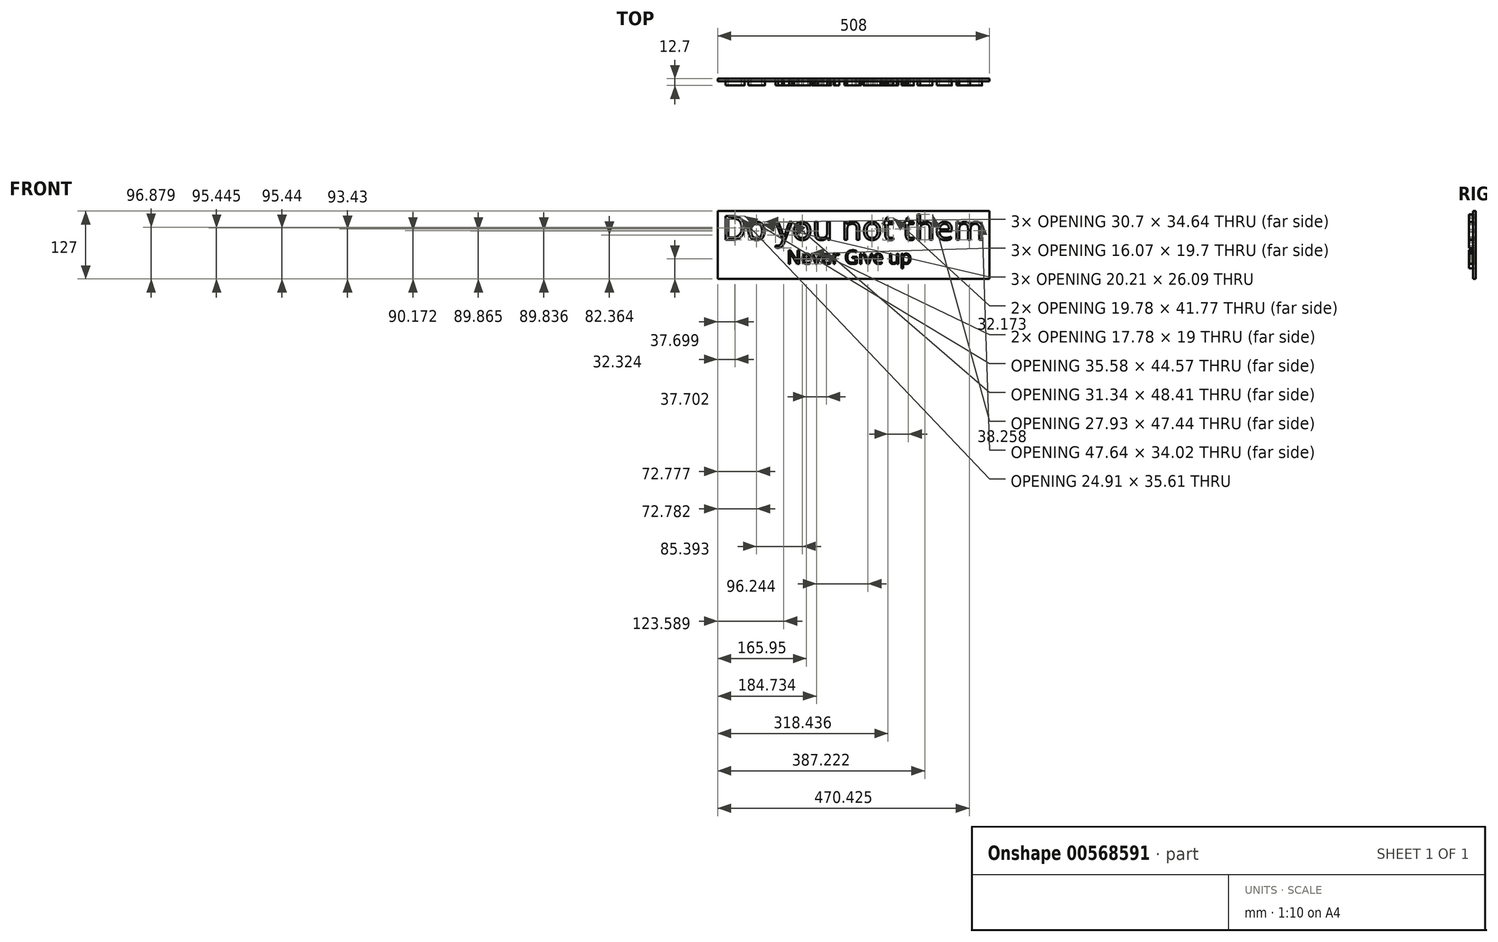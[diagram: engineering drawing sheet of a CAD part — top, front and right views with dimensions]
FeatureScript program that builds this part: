
annotation { "Feature Type Name" : "Feature", "Feature Type Description" : "" }
export const myFeature = defineFeature(function(context is Context, id is Id, definition is map)
    precondition{}
    {
        {
            var Q0;
            Q0=qCreatedBy(makeId("Front.planeOp"),FACE);
            var sketch = newSketch(context, id + "F0", { "sketchPlane" : qUnion([Q0])});
            skLineSegment(sketch, "E0", {"start": v(0, 0) * mm, "end": v(254, 0) * mm});
            skLineSegment(sketch, "E1", {"start": v(0, 0) * mm, "end": v(-254, 0) * mm});
            skLineSegment(sketch, "E2", {"start": v(254, 0) * mm, "end": v(254, 127) * mm});
            skLineSegment(sketch, "E3", {"start": v(254, 127) * mm, "end": v(-254, 127) * mm});
            skLineSegment(sketch, "E4", {"start": v(-254, 0) * mm, "end": v(-254, 127) * mm});
            skText(sketch, "E5", { "text": "Do you not them\n", "fontName": "OpenSans-Regular.ttf"});
            skText(sketch, "E6", { "text": "Never Give up", "fontName": "OpenSans-Regular.ttf"});
            const initialGuessF0  = {"E5": [-0.24559, 0.07316, 1, 0, 0.04495], "E6": [-0.12484, 0.0282, 1, 0, 0.02556]};
            skSetInitialGuess(sketch, initialGuessF0);
            skSolve(sketch);
        }
        {
            var Q0;
            Q0=makeQuery(id+"F0.imprint","IMPRINT",FACE,{"disambiguationData":[TD([[makeQuery(id+"F0.imprint","IMPRINT",EDGE,{"derivedFrom":sQuery(id+"F0.wireOp",EDGE,"E5.sketch_text.stroke-0")}),-1.0]])]});
            var Q1;
            Q1=makeQuery(id+"F0.imprint","IMPRINT",FACE,{"disambiguationData":[TD([[makeQuery(id+"F0.imprint","IMPRINT",EDGE,{"derivedFrom":sQuery(id+"F0.wireOp",EDGE,"E5.sketch_text.stroke-14")}),-1.0]])]});
            var Q2;
            Q2=makeQuery(id+"F0.imprint","IMPRINT",FACE,{"disambiguationData":[TD([[makeQuery(id+"F0.imprint","IMPRINT",EDGE,{"derivedFrom":sQuery(id+"F0.wireOp",EDGE,"E5.sketch_text.stroke-31")}),-1.0]])]});
            var Q3;
            Q3=makeQuery(id+"F0.imprint","IMPRINT",FACE,{"disambiguationData":[TD([[makeQuery(id+"F0.imprint","IMPRINT",EDGE,{"derivedFrom":sQuery(id+"F0.wireOp",EDGE,"E5.sketch_text.stroke-47")}),-1.0]])]});
            var Q4;
            Q4=makeQuery(id+"F0.imprint","IMPRINT",FACE,{"disambiguationData":[TD([[makeQuery(id+"F0.imprint","IMPRINT",EDGE,{"derivedFrom":sQuery(id+"F0.wireOp",EDGE,"E5.sketch_text.stroke-64")}),-1.0]])]});
            var Q5;
            Q5=makeQuery(id+"F0.imprint","IMPRINT",FACE,{"disambiguationData":[TD([[makeQuery(id+"F0.imprint","IMPRINT",EDGE,{"derivedFrom":sQuery(id+"F0.wireOp",EDGE,"E5.sketch_text.stroke-81")}),-1.0]])]});
            var Q6;
            Q6=makeQuery(id+"F0.imprint","IMPRINT",FACE,{"disambiguationData":[TD([[makeQuery(id+"F0.imprint","IMPRINT",EDGE,{"derivedFrom":sQuery(id+"F0.wireOp",EDGE,"E5.sketch_text.stroke-98")}),-1.0]])]});
            var Q7;
            Q7=makeQuery(id+"F0.imprint","IMPRINT",FACE,{"disambiguationData":[TD([[makeQuery(id+"F0.imprint","IMPRINT",EDGE,{"derivedFrom":sQuery(id+"F0.wireOp",EDGE,"E5.sketch_text.stroke-115")}),-1.0]])]});
            var Q8;
            Q8=makeQuery(id+"F0.imprint","IMPRINT",FACE,{"disambiguationData":[TD([[makeQuery(id+"F0.imprint","IMPRINT",EDGE,{"derivedFrom":sQuery(id+"F0.wireOp",EDGE,"E5.sketch_text.stroke-134")}),-1.0]])]});
            var Q9;
            Q9=makeQuery(id+"F0.imprint","IMPRINT",FACE,{"disambiguationData":[TD([[makeQuery(id+"F0.imprint","IMPRINT",EDGE,{"derivedFrom":sQuery(id+"F0.wireOp",EDGE,"E5.sketch_text.stroke-153")}),-1.0]])]});
            var Q10;
            Q10=makeQuery(id+"F0.imprint","IMPRINT",FACE,{"disambiguationData":[TD([[makeQuery(id+"F0.imprint","IMPRINT",EDGE,{"derivedFrom":sQuery(id+"F0.wireOp",EDGE,"E5.sketch_text.stroke-171")}),-1.0]])]});
            var Q11;
            Q11=makeQuery(id+"F0.imprint","IMPRINT",FACE,{"disambiguationData":[TD([[makeQuery(id+"F0.imprint","IMPRINT",EDGE,{"derivedFrom":sQuery(id+"F0.wireOp",EDGE,"E5.sketch_text.stroke-190")}),-1.0]])]});
            extrude(context, id + "F1", {"entities" : qUnion([Q0, Q1, Q2, Q3, Q4, Q5, Q6, Q7, Q8, Q9, Q10, Q11]), "oppositeDirection" : true, "depth" : -12.7 * mm, "offsetDistance" : 25.4 * mm});
        }
        {
            var Q0;
            Q0=makeQuery(id+"F0.imprint","IMPRINT",FACE,{"disambiguationData":[TD([[makeQuery(id+"F0.imprint","IMPRINT",EDGE,{"derivedFrom":sQuery(id+"F0.wireOp",EDGE,"E6.sketch_text.stroke-0")}),-1.0]])]});
            var Q1;
            Q1=makeQuery(id+"F0.imprint","IMPRINT",FACE,{"disambiguationData":[TD([[makeQuery(id+"F0.imprint","IMPRINT",EDGE,{"derivedFrom":sQuery(id+"F0.wireOp",EDGE,"E6.sketch_text.stroke-15")}),-1.0]])]});
            var Q2;
            Q2=makeQuery(id+"F0.imprint","IMPRINT",FACE,{"disambiguationData":[TD([[makeQuery(id+"F0.imprint","IMPRINT",EDGE,{"derivedFrom":sQuery(id+"F0.wireOp",EDGE,"E6.sketch_text.stroke-34")}),-1.0]])]});
            var Q3;
            Q3=makeQuery(id+"F0.imprint","IMPRINT",FACE,{"disambiguationData":[TD([[makeQuery(id+"F0.imprint","IMPRINT",EDGE,{"derivedFrom":sQuery(id+"F0.wireOp",EDGE,"E6.sketch_text.stroke-44")}),-1.0]])]});
            var Q4;
            Q4=makeQuery(id+"F0.imprint","IMPRINT",FACE,{"disambiguationData":[TD([[makeQuery(id+"F0.imprint","IMPRINT",EDGE,{"derivedFrom":sQuery(id+"F0.wireOp",EDGE,"E6.sketch_text.stroke-63")}),-1.0]])]});
            var Q5;
            Q5=makeQuery(id+"F0.imprint","IMPRINT",FACE,{"disambiguationData":[TD([[makeQuery(id+"F0.imprint","IMPRINT",EDGE,{"derivedFrom":sQuery(id+"F0.wireOp",EDGE,"E6.sketch_text.stroke-76")}),-1.0]])]});
            var Q6;
            Q6=makeQuery(id+"F0.imprint","IMPRINT",FACE,{"disambiguationData":[TD([[makeQuery(id+"F0.imprint","IMPRINT",EDGE,{"derivedFrom":sQuery(id+"F0.wireOp",EDGE,"E6.sketch_text.stroke-96")}),-1.0]])]});
            var Q7;
            Q7=makeQuery(id+"F0.imprint","IMPRINT",FACE,{"disambiguationData":[TD([[makeQuery(id+"F0.imprint","IMPRINT",EDGE,{"derivedFrom":sQuery(id+"F0.wireOp",EDGE,"E6.sketch_text.stroke-108")}),-1.0]])]});
            var Q8;
            Q8=makeQuery(id+"F0.imprint","IMPRINT",FACE,{"disambiguationData":[TD([[makeQuery(id+"F0.imprint","IMPRINT",EDGE,{"derivedFrom":sQuery(id+"F0.wireOp",EDGE,"E6.sketch_text.stroke-118")}),-1.0]])]});
            var Q9;
            Q9=makeQuery(id+"F0.imprint","IMPRINT",FACE,{"disambiguationData":[TD([[makeQuery(id+"F0.imprint","IMPRINT",EDGE,{"derivedFrom":sQuery(id+"F0.wireOp",EDGE,"E6.sketch_text.stroke-137")}),-1.0]])]});
            var Q10;
            Q10=makeQuery(id+"F0.imprint","IMPRINT",FACE,{"disambiguationData":[TD([[makeQuery(id+"F0.imprint","IMPRINT",EDGE,{"derivedFrom":sQuery(id+"F0.wireOp",EDGE,"E6.sketch_text.stroke-154")}),-1.0]])]});
            extrude(context, id + "F2", {"entities" : qUnion([Q0, Q1, Q2, Q3, Q4, Q5, Q6, Q7, Q8, Q9, Q10]), "depth" : 12.7 * mm, "offsetDistance" : 25.4 * mm});
        }
        {
            var Q0;
            Q0=makeQuery(id+"F0.imprint","IMPRINT",FACE,{"disambiguationData":[TD([[makeQuery(id+"F0.imprint","IMPRINT",EDGE,{"derivedFrom":sQuery(id+"F0.wireOp",EDGE,"E0")}),1.0]])]});
            var Q1;
            Q1=makeQuery(id+"F0.imprint","IMPRINT",FACE,{"disambiguationData":[TD([[makeQuery(id+"F0.imprint","IMPRINT",EDGE,{"derivedFrom":sQuery(id+"F0.wireOp",EDGE,"E5.sketch_text.stroke-7")}),1.0]])]});
            var Q2;
            Q2=makeQuery(id+"F0.imprint","IMPRINT",FACE,{"disambiguationData":[TD([[makeQuery(id+"F0.imprint","IMPRINT",EDGE,{"derivedFrom":sQuery(id+"F0.wireOp",EDGE,"E5.sketch_text.stroke-23")}),1.0]])]});
            var Q3;
            Q3=makeQuery(id+"F0.imprint","IMPRINT",FACE,{"disambiguationData":[TD([[makeQuery(id+"F0.imprint","IMPRINT",EDGE,{"derivedFrom":sQuery(id+"F0.wireOp",EDGE,"E5.sketch_text.stroke-56")}),1.0]])]});
            var Q4;
            Q4=makeQuery(id+"F0.imprint","IMPRINT",FACE,{"disambiguationData":[TD([[makeQuery(id+"F0.imprint","IMPRINT",EDGE,{"derivedFrom":sQuery(id+"F0.wireOp",EDGE,"E5.sketch_text.stroke-107")}),1.0]])]});
            var Q5;
            Q5=makeQuery(id+"F0.imprint","IMPRINT",FACE,{"disambiguationData":[TD([[makeQuery(id+"F0.imprint","IMPRINT",EDGE,{"derivedFrom":sQuery(id+"F0.wireOp",EDGE,"E6.sketch_text.stroke-29")}),1.0]])]});
            var Q6;
            Q6=makeQuery(id+"F0.imprint","IMPRINT",FACE,{"disambiguationData":[TD([[makeQuery(id+"F0.imprint","IMPRINT",EDGE,{"derivedFrom":sQuery(id+"F0.wireOp",EDGE,"E6.sketch_text.stroke-58")}),1.0]])]});
            var Q7;
            Q7=makeQuery(id+"F0.imprint","IMPRINT",FACE,{"disambiguationData":[TD([[makeQuery(id+"F0.imprint","IMPRINT",EDGE,{"derivedFrom":sQuery(id+"F0.wireOp",EDGE,"E6.sketch_text.stroke-170")}),1.0]])]});
            var Q8;
            Q8=makeQuery(id+"F0.imprint","IMPRINT",FACE,{"disambiguationData":[TD([[makeQuery(id+"F0.imprint","IMPRINT",EDGE,{"derivedFrom":sQuery(id+"F0.wireOp",EDGE,"E6.sketch_text.stroke-132")}),1.0]])]});
            var Q9;
            Q9=makeQuery(id+"F0.imprint","IMPRINT",FACE,{"disambiguationData":[TD([[makeQuery(id+"F0.imprint","IMPRINT",EDGE,{"derivedFrom":sQuery(id+"F0.wireOp",EDGE,"E6.sketch_text.stroke-100")}),-1.0]])]});
            var Q10;
            Q10=makeQuery(id+"F0.imprint","IMPRINT",FACE,{"disambiguationData":[TD([[makeQuery(id+"F0.imprint","IMPRINT",EDGE,{"derivedFrom":sQuery(id+"F0.wireOp",EDGE,"E5.sketch_text.stroke-185")}),1.0]])]});
            extrude(context, id + "F3", {"entities" : qUnion([Q0, Q1, Q2, Q3, Q4, Q5, Q6, Q7, Q8, Q9, Q10]), "depth" : 5.08 * mm, "offsetDistance" : 25.4 * mm});
        }
    });
